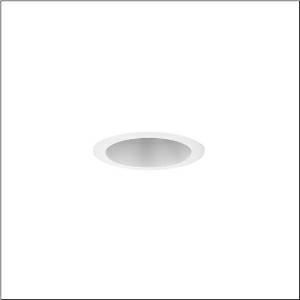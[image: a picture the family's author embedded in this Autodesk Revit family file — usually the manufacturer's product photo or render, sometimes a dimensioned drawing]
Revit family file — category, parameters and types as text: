
# Revit family: lunis_31-l_51dn16ee41b
name_source: partatom
category: Lighting Fixtures
units: mm (PartAtom-declared; Revit-internal decimal feet)

## family parameters
Cut with Voids When Loaded = No
Host = Face
Light Source = No
Part Type = Normal
Room Calculation Point = No
Round Connector Dimension = Use Diameter
Shared = No

## types (1)
- --- (1 x LED, 1600 lm, 12 W, 4000K)
    Apparent Load = 12 VA
    CIE Flux Codes = 76 93 99 100 100
    Color Rendering = 80
    Color Temperature = 4000K
    Default Elevation = 1800 mm
    Description = Lunis 31, -L, downlight, light control with reflector, light emission: direct distribution, LED rated luminous flux: 1.600lm, light colour: 840, mains connection: 220..240V, AC, 50/60Hz, housing, of aluminium, white, protection rating (complete): IP20, protection rating (on room side): IP54, insulation class (complete): insulation class II (safety insulation), certification: CE, packaging unit: 1 piece
    Height = 0 mm  [stored 0 ft]
    Lamp = 1 x LED
    Lamp Light Flux = 1600 lm
    Lamp Power = 12 W
    Lamp count = 1
    Length = 188 mm  [stored 0.616798 ft]
    Luminous efficacy = 133 lm/W
    Manufacturer = Siteco
    ModVariant = No
    Model = 51DN16EE41B
    Mounting Place = Ceiling
    Mounting Type = Recessed
    Number of Poles = 1
    OnlyDefault = Yes
    Power Factor = 1
    Product Name = Lunis 31-L
    Product group = downlight
    ProductGroupID = 400
    Protection Class = Protection class II
    Protection Degree = IP 20
    RLX_Detail_Level = 1
    RLX_Emergency_Light_Flux = 0 lm
    RLX_Emergency_Type = 0
    RLX_Emergency_Type_DB = No
    RlxData = <blob elided: 22501 chars, md5=1bcf4dbd>
    Socket = socket
    Standby Power = 0 W
    System Light Flux = 1600 lm
    System Power = 12 W
    Type Comments = individual setting: luminous flux: 100 % | (OFF | ON) | 300 mA
    Type Image = l_1345911.jpg
    URL = http://relux.com
    VarID = @adj_010155
    Voltage = 0 V
    Weight = 0.00 kg
    Width = 0 mm  [stored 0 ft]

note: [stored X ft] marks values corroborated as IEEE doubles in the binary element streams (Revit-internal decimal feet)

## geometry (parser evidence)
native form markers: Blend x4, Sweep x10
no freeform markers — native parametric forms only
